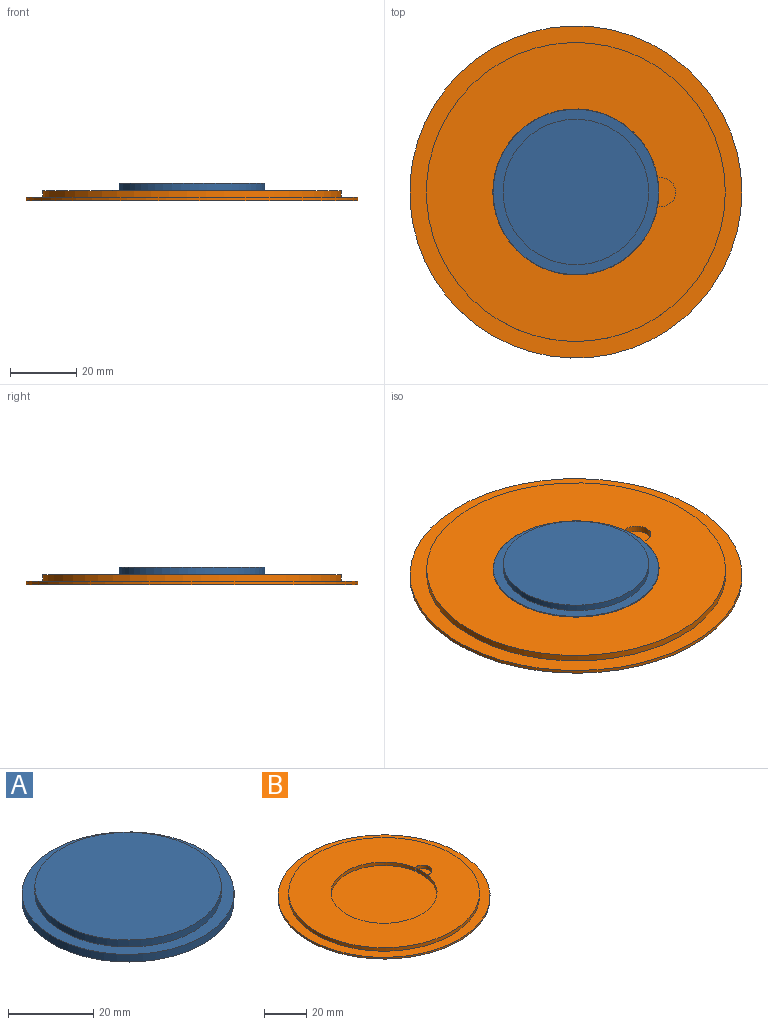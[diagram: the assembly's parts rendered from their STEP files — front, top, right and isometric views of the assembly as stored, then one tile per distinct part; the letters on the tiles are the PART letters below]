
ASSEMBLY  parts=2 mates=1
PART A: 5 faces, bbox 49.8x49.8x4.2 mm
  f0: plane 49.8x49.8mm, normal (0,0,-1), area 1947.8mm2, adj f4
  f1: plane 43.8x43.8mm, normal (0,0,1), area 1506.7mm2, adj f2
  f2: cylinder r=21.9mm len=43.8mm, axis (0,0,1), area 275.2mm2, adj f1,f3
  f3: plane 49.8x49.8mm, normal (0,0,1), area 441.1mm2, adj f2,f4
  f4: cylinder r=24.9mm len=49.8mm, axis (0,0,1), area 344.2mm2, adj f0,f3
PART B: 9 faces, bbox 100x100x3 mm
  f0: cylinder r=25mm len=50mm, axis (0,0,1), area 312.5mm2, adj f2,f6,f7,f8
  f1: plane 100x100mm, normal (0,0,-1), area 7854mm2, adj f5
  f2: plane 90x90mm, normal (0,0,1), area 4362mm2, adj f0,f3,f7,f8
  f3: cylinder r=45mm len=90mm, axis (0,0,1), area 565.5mm2, adj f2,f4
  f4: plane 100x100mm, normal (0,0,1), area 1492.3mm2, adj f3,f5
  f5: cylinder r=50mm len=100mm, axis (0,0,1), area 314.2mm2, adj f1,f4
  f6: plane 55.05x50mm, normal (0,0,1), area 1999.7mm2, adj f0,f7,f8
  f7: cylinder r=22.46mm len=7.52mm, axis (0,0,1), area 15.1mm2, adj f0,f2,f6,f8
  f8: cylinder r=4.31mm len=8.63mm, axis (0,0,1), area 31.4mm2, adj f0,f2,f6,f7
PLACE A t=(-8.73,-7.7,-5.09)mm
PLACE B t=(-8.73,-7.7,-6.09)mm
MATE parallel A.f2 <-> B.f6  axis (0,0,-1) through (-8.73,-7.7,-5.09)mm
